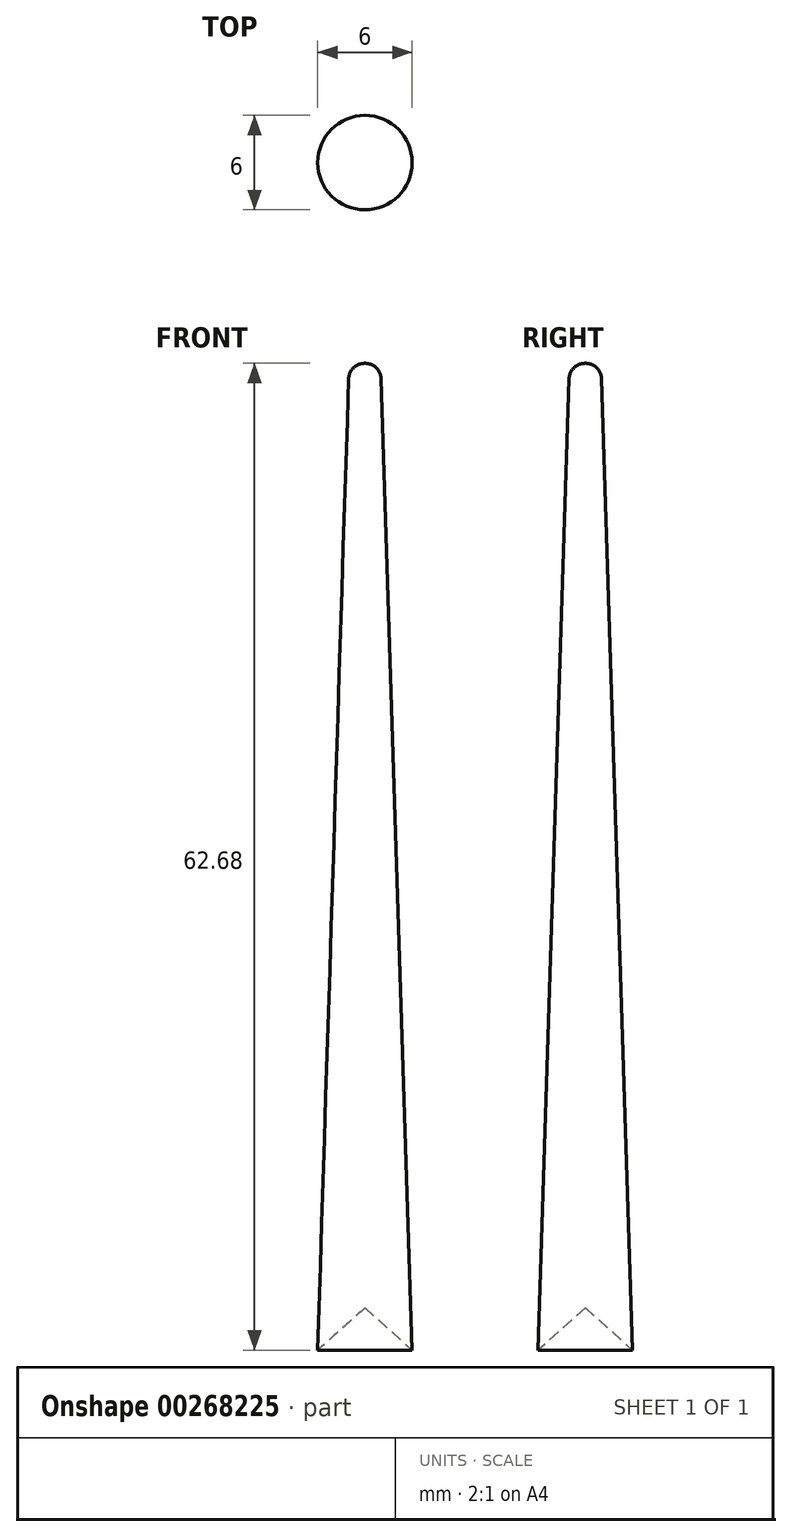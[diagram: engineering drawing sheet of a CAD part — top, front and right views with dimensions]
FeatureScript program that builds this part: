
annotation { "Feature Type Name" : "Feature", "Feature Type Description" : "" }
export const myFeature = defineFeature(function(context is Context, id is Id, definition is map)
    precondition{}
    {
        {
            var Q0;
            Q0=qCreatedBy(makeId("Front.planeOp"),FACE);
            var sketch = newSketch(context, id + "F0", { "sketchPlane" : qUnion([Q0])});
            skLineSegment(sketch, "E0", {"start": v(0, 0) * mm, "end": v(0, 60) * mm});
            skLineSegment(sketch, "E1", {"start": v(0, 60) * mm, "end": v(0.03, 60) * mm});
            skLineSegment(sketch, "E2", {"start": v(1.03, 59.03) * mm, "end": v(3, -2.68) * mm});
            skLineSegment(sketch, "E3", {"start": v(3, -2.68) * mm, "end": v(0, 0) * mm});
            skPoint(sketch, "E4.visualSharp", {"position": v(1, 60) * mm});
            skArc(sketch, "E4.filletArc", {"start": v(1.03, 59.03) * mm, "mid": v(0.73, 59.72) * mm, "end": v(0.03, 60) * mm});
            skSolve(sketch);
        }
        {
            var Q0;
            Q0=makeQuery(id+"F0.imprint","IMPRINT",FACE,{"disambiguationData":[TD([[makeQuery(id+"F0.imprint","IMPRINT",EDGE,{"derivedFrom":sQuery(id+"F0.wireOp",EDGE,"E0")}),-1.0]])]});
            var Q1;
            Q1=sQuery(id+"F0.wireOp",EDGE,"E0");
            revolve(context, id + "F1", {"entities" : qUnion([Q0]), "axis" : qUnion([Q1]), "revolveType" : RevolveType.FULL});
        }
    });
